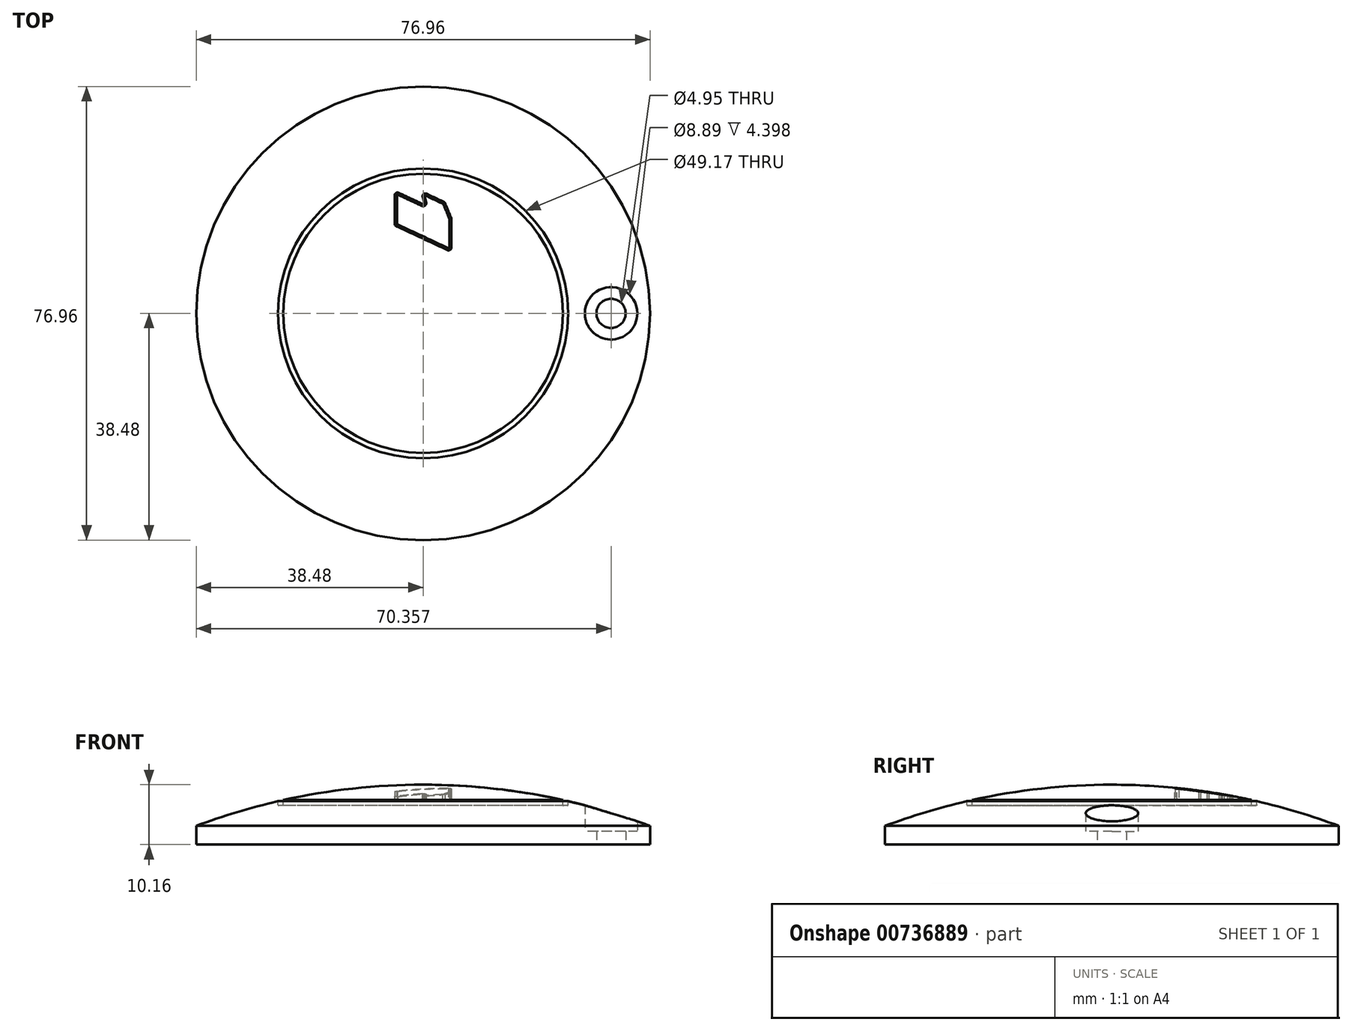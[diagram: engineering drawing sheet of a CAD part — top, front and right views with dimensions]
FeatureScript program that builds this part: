
annotation { "Feature Type Name" : "Feature", "Feature Type Description" : "" }
export const myFeature = defineFeature(function(context is Context, id is Id, definition is map)
    precondition{}
    {
        {
            var Q0;
            Q0=qCreatedBy(makeId("Front.planeOp"),FACE);
            var sketch = newSketch(context, id + "F0", { "sketchPlane" : qUnion([Q0])});
            skArc(sketch, "E0", {"start": v(0, 109.5) * mm, "mid": v(-19.55, 107.73) * mm, "end": v(-38.48, 102.5) * mm});
            skLineSegment(sketch, "E1", {"start": v(-38.48, 99.33) * mm, "end": v(0, 99.33) * mm});
            skLineSegment(sketch, "E2", {"start": v(0, 109.5) * mm, "end": v(0, 0) * mm});
            skLineSegment(sketch, "E3", {"start": v(0, 0) * mm, "end": v(0, 99.33) * mm});
            skLineSegment(sketch, "E4", {"start": v(-38.48, 102.5) * mm, "end": v(-38.48, 99.33) * mm});
            skPoint(sketch, "E5.orphan", {"position": v(46.06, 99.33) * mm});
            skPoint(sketch, "E6.orphan", {"position": v(-46.06, 99.33) * mm});
            skSolve(sketch);
        }
        {
            var Q0;
            Q0=makeQuery(id+"F0.imprint","IMPRINT",FACE,{"disambiguationData":[TD([[makeQuery(id+"F0.imprint","IMPRINT",EDGE,{"derivedFrom":sQuery(id+"F0.wireOp",EDGE,"E0")}),1.0]])]});
            var Q1;
            Q1=sQuery(id+"F0.wireOp",EDGE,"E2");
            revolve(context, id + "F1", {"surfaceOperationType" : NewSurfaceOperationType.NEW, "entities" : qUnion([Q0]), "axis" : qUnion([Q1]), "revolveType" : RevolveType.FULL});
        }
        {
            var Q0;
            Q0=makeQuery(id+"F1.opRevolve","SWEPT_FACE",FACE,{"disambiguationData":[OSD([sQuery(id+"F0.wireOp",EDGE,"E1")])]});
            var sketch = newSketch(context, id + "F2", { "sketchPlane" : qUnion([Q0])});
            skCircle(sketch, "E7", {"center": v(31.88, 0) * mm, "radius": 2.48 * mm});
            skSolve(sketch);
        }
        {
            var Q0;
            Q0 = qSketchRegion(id + "F2", true);
            extrude(context, id + "F3", {"entities" : qUnion([Q0]), "operationType" : NewBodyOperationType.REMOVE, "endBound" : BoundingType.THROUGH_ALL, "oppositeDirection" : true, "depth" : 25.4 * mm, "offsetDistance" : 25.4 * mm});
        }
        {
            var Q0;
            Q0=qCreatedBy(makeId("Top.planeOp"),FACE);
            cPlane(context, id + "F4", {"entities" : qUnion([Q0]), "cplaneType" : CPlaneType.OFFSET, "offset" : 101.6 * mm, "width" : 152.4 * mm, "height" : 152.4 * mm});
        }
        {
            var Q0;
            Q0=qCreatedBy(id+"F4.planeOp",FACE);
            var sketch = newSketch(context, id + "F5", { "sketchPlane" : qUnion([Q0])});
            skCircle(sketch, "E8", {"center": v(31.88, 0) * mm, "radius": 4.45 * mm});
            skSolve(sketch);
        }
        {
            var Q0;
            Q0 = qSketchRegion(id + "F5", true);
            extrude(context, id + "F6", {"entities" : qUnion([Q0]), "operationType" : NewBodyOperationType.REMOVE, "depth" : 25.4 * mm, "offsetDistance" : 25.4 * mm});
        }
        {
            var Q0;
            Q0=qCreatedBy(makeId("Right.planeOp"),FACE);
            var sketch = newSketch(context, id + "F7", { "sketchPlane" : qUnion([Q0])});
            skLineSegment(sketch, "E9", {"start": v(0, 0) * mm, "end": v(0, 121.84) * mm});
            skSolve(sketch);
        }
        {
            var Q0;
            Q0=qCreatedBy(makeId("Right.planeOp"),FACE);
            var sketch = newSketch(context, id + "F8", { "sketchPlane" : qUnion([Q0])});
            skLineSegment(sketch, "E10.bottom", {"start": v(23.7, 116.08) * mm, "end": v(24.59, 116.08) * mm});
            skLineSegment(sketch, "E10.top", {"start": v(23.83, 105.93) * mm, "end": v(24.46, 105.93) * mm});
            skLineSegment(sketch, "E10.left", {"start": v(23.7, 116.08) * mm, "end": v(23.7, 106.06) * mm});
            skLineSegment(sketch, "E10.right", {"start": v(24.59, 116.08) * mm, "end": v(24.59, 106.06) * mm});
            skPoint(sketch, "E11.visualSharp", {"position": v(23.7, 105.93) * mm});
            skArc(sketch, "E11.filletArc", {"start": v(23.7, 106.06) * mm, "mid": v(23.74, 105.97) * mm, "end": v(23.83, 105.93) * mm});
            skPoint(sketch, "E12.visualSharp", {"position": v(24.59, 105.93) * mm});
            skArc(sketch, "E12.filletArc", {"start": v(24.46, 105.93) * mm, "mid": v(24.55, 105.97) * mm, "end": v(24.59, 106.06) * mm});
            skLineSegment(sketch, "E13", {"start": v(0, 76.23) * mm, "end": v(0, 117.25) * mm});
            skSolve(sketch);
        }
        {
            var Q0;
            Q0 = qSketchRegion(id + "F8", true);
            var Q1;
            Q1=sQuery(id+"F8.wireOp",EDGE,"E13");
            revolve(context, id + "F9", {"operationType" : NewBodyOperationType.REMOVE, "surfaceOperationType" : NewSurfaceOperationType.NEW, "entities" : qUnion([Q0]), "axis" : qUnion([Q1]), "revolveType" : RevolveType.ONE_DIRECTION, "oppositeDirection" : true, "angle" : 360 * degree});
        }
        {
            var Q0;
            Q0=qCreatedBy(id+"F4.planeOp",FACE);
            cPlane(context, id + "F10", {"entities" : qUnion([Q0]), "cplaneType" : CPlaneType.OFFSET, "offset" : 25.4 * mm, "width" : 152.4 * mm, "height" : 152.4 * mm});
        }
        {
            var Q0;
            Q0=qCreatedBy(id+"F10.planeOp",FACE);
            var sketch = newSketch(context, id + "F11", { "sketchPlane" : qUnion([Q0])});
            skLineSegment(sketch, "E14", {"start": v(-4.45, 20) * mm, "end": v(-4.45, 15.2) * mm});
            skLineSegment(sketch, "E15", {"start": v(-4.37, 15.1) * mm, "end": v(4.26, 11.07) * mm});
            skLineSegment(sketch, "E16", {"start": v(4.44, 11.18) * mm, "end": v(4.44, 15.99) * mm});
            skLineSegment(sketch, "E17", {"start": v(4.42, 16.13) * mm, "end": v(3.46, 18.45) * mm});
            skLineSegment(sketch, "E18", {"start": v(0.29, 19.81) * mm, "end": v(0.52, 18.8) * mm});
            skLineSegment(sketch, "E19", {"start": v(-0.19, 18.22) * mm, "end": v(-4.26, 20.12) * mm});
            skLineSegment(sketch, "E20", {"start": v(0.46, 19.96) * mm, "end": v(3.27, 18.65) * mm});
            skPoint(sketch, "E21.visualSharp", {"position": v(0.76, 17.78) * mm});
            skArc(sketch, "E21.filletArc", {"start": v(-0.19, 18.22) * mm, "mid": v(0.35, 18.29) * mm, "end": v(0.52, 18.8) * mm});
            skPoint(sketch, "E22.visualSharp", {"position": v(3.4, 18.58) * mm});
            skArc(sketch, "E22.filletArc", {"start": v(3.46, 18.45) * mm, "mid": v(3.39, 18.56) * mm, "end": v(3.27, 18.65) * mm});
            skPoint(sketch, "E23.visualSharp", {"position": v(4.44, 16.06) * mm});
            skArc(sketch, "E23.filletArc", {"start": v(4.44, 15.99) * mm, "mid": v(4.44, 16.06) * mm, "end": v(4.42, 16.13) * mm});
            skPoint(sketch, "E24.visualSharp", {"position": v(4.44, 10.98) * mm});
            skArc(sketch, "E24.filletArc", {"start": v(4.26, 11.07) * mm, "mid": v(4.39, 11.07) * mm, "end": v(4.44, 11.18) * mm});
            skPoint(sketch, "E25.visualSharp", {"position": v(-4.45, 15.13) * mm});
            skArc(sketch, "E25.filletArc", {"start": v(-4.45, 15.2) * mm, "mid": v(-4.43, 15.14) * mm, "end": v(-4.37, 15.1) * mm});
            skPoint(sketch, "E26.visualSharp", {"position": v(-4.45, 20.2) * mm});
            skArc(sketch, "E26.filletArc", {"start": v(-4.26, 20.12) * mm, "mid": v(-4.39, 20.12) * mm, "end": v(-4.45, 20) * mm});
            skPoint(sketch, "E27.visualSharp", {"position": v(0.23, 20.07) * mm});
            skArc(sketch, "E27.filletArc", {"start": v(0.46, 19.96) * mm, "mid": v(0.33, 19.94) * mm, "end": v(0.29, 19.81) * mm});
            skLineSegment(sketch, "E28", {"start": v(-4.45, 9.14) * mm, "end": v(-4.45, 4.34) * mm});
            skLineSegment(sketch, "E29", {"start": v(-4.37, 4.23) * mm, "end": v(4.26, 0.2) * mm});
            skLineSegment(sketch, "E30", {"start": v(4.45, 0.32) * mm, "end": v(4.45, 5.12) * mm});
            skLineSegment(sketch, "E31", {"start": v(4.42, 5.27) * mm, "end": v(3.42, 7.68) * mm});
            skLineSegment(sketch, "E32", {"start": v(0.44, 8.97) * mm, "end": v(0.73, 7.15) * mm});
            skLineSegment(sketch, "E33", {"start": v(0.55, 7.02) * mm, "end": v(-4.26, 9.26) * mm});
            skLineSegment(sketch, "E34", {"start": v(0.62, 9.1) * mm, "end": v(3.23, 7.88) * mm});
            skPoint(sketch, "E35.visualSharp", {"position": v(0.76, 6.91) * mm});
            skArc(sketch, "E35.filletArc", {"start": v(0.55, 7.02) * mm, "mid": v(0.68, 7.03) * mm, "end": v(0.73, 7.15) * mm});
            skPoint(sketch, "E36.visualSharp", {"position": v(3.36, 7.82) * mm});
            skArc(sketch, "E36.filletArc", {"start": v(3.42, 7.68) * mm, "mid": v(3.34, 7.8) * mm, "end": v(3.23, 7.88) * mm});
            skPoint(sketch, "E37.visualSharp", {"position": v(4.45, 5.2) * mm});
            skArc(sketch, "E37.filletArc", {"start": v(4.45, 5.12) * mm, "mid": v(4.44, 5.2) * mm, "end": v(4.42, 5.27) * mm});
            skPoint(sketch, "E38.visualSharp", {"position": v(4.45, 0.12) * mm});
            skArc(sketch, "E38.filletArc", {"start": v(4.26, 0.2) * mm, "mid": v(4.39, 0.2) * mm, "end": v(4.45, 0.32) * mm});
            skPoint(sketch, "E39.visualSharp", {"position": v(-4.45, 4.26) * mm});
            skArc(sketch, "E39.filletArc", {"start": v(-4.45, 4.34) * mm, "mid": v(-4.43, 4.28) * mm, "end": v(-4.37, 4.23) * mm});
            skPoint(sketch, "E40.visualSharp", {"position": v(-4.45, 9.34) * mm});
            skArc(sketch, "E40.filletArc", {"start": v(-4.26, 9.26) * mm, "mid": v(-4.39, 9.25) * mm, "end": v(-4.45, 9.14) * mm});
            skPoint(sketch, "E41.visualSharp", {"position": v(0.4, 9.2) * mm});
            skArc(sketch, "E41.filletArc", {"start": v(0.62, 9.1) * mm, "mid": v(0.5, 9.09) * mm, "end": v(0.44, 8.97) * mm});
            skLineSegment(sketch, "E42", {"start": v(1.15, -0.88) * mm, "end": v(-1.37, 0.3) * mm});
            skLineSegment(sketch, "E43", {"start": v(-4.45, -1.67) * mm, "end": v(-4.44, -7.74) * mm});
            skLineSegment(sketch, "E44", {"start": v(-0.78, -13.5) * mm, "end": v(1.01, -14.33) * mm});
            skLineSegment(sketch, "E45", {"start": v(4.45, -12.15) * mm, "end": v(4.45, -6.06) * mm});
            skPoint(sketch, "E46.visualSharp", {"position": v(4.45, -15.94) * mm});
            skArc(sketch, "E46.filletArc", {"start": v(4.25, -15.85) * mm, "mid": v(4.38, -15.83) * mm, "end": v(4.43, -15.73) * mm});
            skPoint(sketch, "E47.visualSharp", {"position": v(-4.44, -11.79) * mm});
            skArc(sketch, "E47.filletArc", {"start": v(-4.44, -7.74) * mm, "mid": v(-3.45, -11.16) * mm, "end": v(-0.78, -13.5) * mm});
            skArc(sketch, "E48.filletArc", {"start": v(1.01, -14.33) * mm, "mid": v(3.33, -14.18) * mm, "end": v(4.45, -12.15) * mm});
            skArc(sketch, "E49.filletArc", {"start": v(-1.37, 0.3) * mm, "mid": v(-3.45, 0.15) * mm, "end": v(-4.44, -1.67) * mm});
            skPoint(sketch, "E50.visualSharp", {"position": v(4.44, -2.42) * mm});
            skArc(sketch, "E50.filletArc", {"start": v(4.44, -6.06) * mm, "mid": v(3.55, -3) * mm, "end": v(1.15, -0.88) * mm});
            skSolve(sketch);
        }
        {
            var Q0;
            Q0=sQuery(id+"F11.wireOp",VERTEX,"E15.start");
            var Q1;
            Q1=qCreatedBy(makeId("Right.planeOp"),FACE);
            cPlane(context, id + "F12", {"entities" : qUnion([Q0, Q1]), "cplaneType" : CPlaneType.PLANE_POINT, "offset" : 25.4 * mm, "oppositeDirection" : true, "width" : 152.4 * mm, "height" : 152.4 * mm});
        }
        {
            var Q0;
            Q0=qCreatedBy(id+"F12.planeOp",FACE);
            var sketch = newSketch(context, id + "F13", { "sketchPlane" : qUnion([Q0])});
            skLineSegment(sketch, "E51.bottom", {"start": v(15.1, 127) * mm, "end": v(14.71, 127) * mm});
            skLineSegment(sketch, "E51.top", {"start": v(15.1, 106.68) * mm, "end": v(14.71, 106.68) * mm});
            skLineSegment(sketch, "E51.left", {"start": v(15.1, 127) * mm, "end": v(15.1, 106.68) * mm});
            skLineSegment(sketch, "E51.right", {"start": v(14.71, 127) * mm, "end": v(14.71, 106.68) * mm});
            skSolve(sketch);
        }
        {
            var Q0;
            Q0=makeQuery(id+"F13.imprint","IMPRINT",FACE,{"disambiguationData":[TD([[makeQuery(id+"F13.imprint","IMPRINT",EDGE,{"derivedFrom":sQuery(id+"F13.wireOp",EDGE,"E51.bottom")}),1.0]])]});
            var Q1;
            Q1=sQuery(id+"F11.wireOp",EDGE,"E25.filletArc");
            var Q2;
            Q2=sQuery(id+"F11.wireOp",EDGE,"E14");
            var Q3;
            Q3=sQuery(id+"F11.wireOp",EDGE,"E26.filletArc");
            var Q4;
            Q4=sQuery(id+"F11.wireOp",EDGE,"E19");
            var Q5;
            Q5=sQuery(id+"F11.wireOp",EDGE,"E21.filletArc");
            var Q6;
            Q6=sQuery(id+"F11.wireOp",EDGE,"E18");
            var Q7;
            Q7=sQuery(id+"F11.wireOp",EDGE,"E27.filletArc");
            var Q8;
            Q8=sQuery(id+"F11.wireOp",EDGE,"E20");
            var Q9;
            Q9=sQuery(id+"F11.wireOp",EDGE,"E22.filletArc");
            var Q10;
            Q10=sQuery(id+"F11.wireOp",EDGE,"E17");
            var Q11;
            Q11=sQuery(id+"F11.wireOp",EDGE,"E23.filletArc");
            var Q12;
            Q12=sQuery(id+"F11.wireOp",EDGE,"E16");
            var Q13;
            Q13=sQuery(id+"F11.wireOp",EDGE,"E24.filletArc");
            var Q14;
            Q14=sQuery(id+"F11.wireOp",EDGE,"E15");
            sweep(context, id + "F14", {"operationType" : NewBodyOperationType.REMOVE, "profiles" : qUnion([Q0]), "path" : qUnion([Q1, Q2, Q3, Q4, Q5, Q6, Q7, Q8, Q9, Q10, Q11, Q12, Q13, Q14])});
        }
    });
